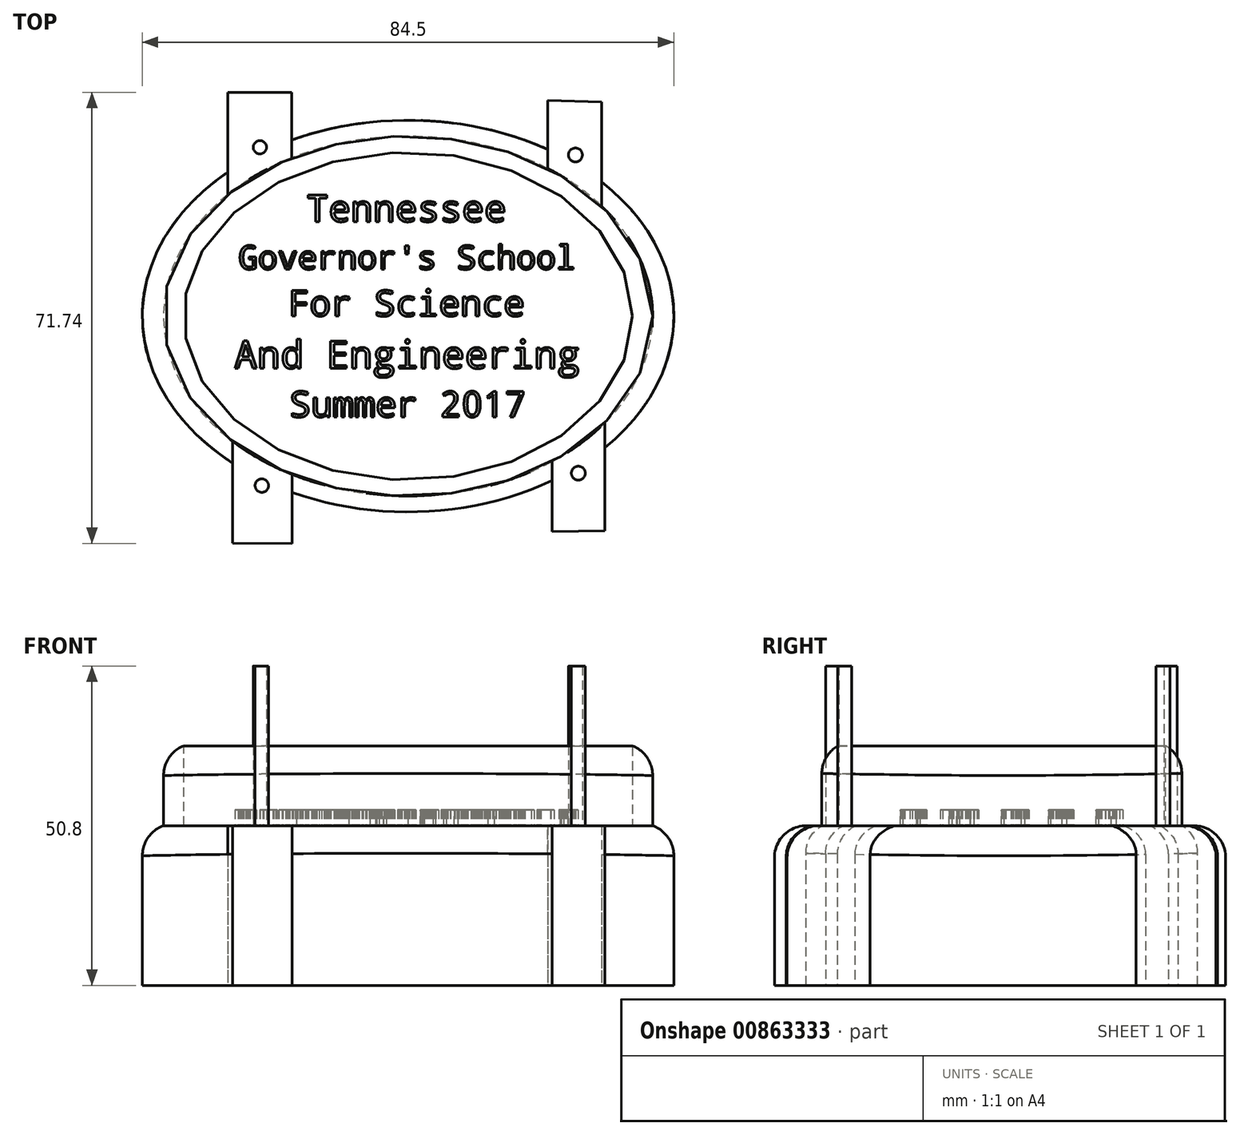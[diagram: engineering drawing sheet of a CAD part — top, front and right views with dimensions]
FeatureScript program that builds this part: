
annotation { "Feature Type Name" : "Feature", "Feature Type Description" : "" }
export const myFeature = defineFeature(function(context is Context, id is Id, definition is map)
    precondition{}
    {
        {
            var Q0;
            Q0=qCreatedBy(makeId("Top.planeOp"),FACE);
            var sketch = newSketch(context, id + "F0", { "sketchPlane" : qUnion([Q0])});
            skEllipse(sketch, "E0", {"center": v(0, 0) * mm, "majorRadius": 42.25 * mm, "minorRadius": 31.15 * mm, "majorAxis": v(1, 0)});
            skLineSegment(sketch, "E1", {"start": v(-28.66, 22.89) * mm, "end": v(-28.66, 35.59) * mm});
            skLineSegment(sketch, "E2", {"start": v(-18.5, 28) * mm, "end": v(-18.5, 35.59) * mm});
            skLineSegment(sketch, "E3", {"start": v(22.23, 26.49) * mm, "end": v(22.23, 34.32) * mm});
            skLineSegment(sketch, "E4", {"start": v(30.75, 21.36) * mm, "end": v(30.75, 34.06) * mm});
            skLineSegment(sketch, "E5", {"start": v(-27.9, -23.39) * mm, "end": v(-27.9, -36.09) * mm});
            skLineSegment(sketch, "E6", {"start": v(-18.43, -28.03) * mm, "end": v(-18.43, -36.15) * mm});
            skLineSegment(sketch, "E7", {"start": v(22.9, -26.17) * mm, "end": v(22.9, -34.3) * mm});
            skLineSegment(sketch, "E8", {"start": v(31.3, -20.93) * mm, "end": v(31.3, -34.14) * mm});
            skLineSegment(sketch, "E9", {"start": v(-28.66, 35.59) * mm, "end": v(-18.5, 35.59) * mm});
            skLineSegment(sketch, "E10", {"start": v(22.23, 34.32) * mm, "end": v(30.75, 34.06) * mm});
            skLineSegment(sketch, "E11", {"start": v(-27.9, -36.09) * mm, "end": v(-18.43, -36.15) * mm});
            skLineSegment(sketch, "E12", {"start": v(22.9, -34.3) * mm, "end": v(31.3, -34.14) * mm});
            skSolve(sketch);
        }
        {
            var Q0;
            {var subQ0=sQuery(id+"F0.wireOp",EDGE,"E0");var subQ4=makeQuery(id+"F0.imprint","INTERSECT",VERTEX,{"derivedFrom":[subQ0,sQuery(id+"F0.wireOp",EDGE,"E3")]});Q0=makeQuery(id+"F0.imprint","IMPRINT",FACE,{"disambiguationData":[TD([[makeQuery(id+"F0.imprint","IMPRINT",EDGE,{"disambiguationData":[TD([[subQ4,1.0]])],"derivedFrom":subQ0}),1.0]])]});}
            var Q1;
            {var subQ0=sQuery(id+"F0.wireOp",EDGE,"E1");Q1=makeQuery(id+"F0.imprint","IMPRINT",FACE,{"disambiguationData":[TD([[makeQuery(id+"F0.imprint","IMPRINT",EDGE,{"derivedFrom":subQ0}),-1.0]])]});}
            var Q2;
            {var subQ0=sQuery(id+"F0.wireOp",EDGE,"E3");Q2=makeQuery(id+"F0.imprint","IMPRINT",FACE,{"disambiguationData":[TD([[makeQuery(id+"F0.imprint","IMPRINT",EDGE,{"derivedFrom":subQ0}),-1.0]])]});}
            var Q3;
            {var subQ0=sQuery(id+"F0.wireOp",EDGE,"E5");Q3=makeQuery(id+"F0.imprint","IMPRINT",FACE,{"disambiguationData":[TD([[makeQuery(id+"F0.imprint","IMPRINT",EDGE,{"derivedFrom":subQ0}),1.0]])]});}
            var Q4;
            {var subQ0=sQuery(id+"F0.wireOp",EDGE,"E7");Q4=makeQuery(id+"F0.imprint","IMPRINT",FACE,{"disambiguationData":[TD([[makeQuery(id+"F0.imprint","IMPRINT",EDGE,{"derivedFrom":subQ0}),1.0]])]});}
            extrude(context, id + "F1", {"entities" : qUnion([Q0, Q1, Q2, Q3, Q4]), "depth" : 25.4 * mm, "offsetDistance" : 25.4 * mm});
        }
        {
            var Q0;
            Q0=makeQuery(id+"F1.opExtrude","CAP_FACE",FACE,{"disambiguationData":[OSD([sQuery(id+"F0.wireOp",EDGE,"E0"),sQuery(id+"F0.wireOp",EDGE,"E1"),sQuery(id+"F0.wireOp",EDGE,"E2"),sQuery(id+"F0.wireOp",EDGE,"E3"),sQuery(id+"F0.wireOp",EDGE,"E4"),sQuery(id+"F0.wireOp",EDGE,"E5"),sQuery(id+"F0.wireOp",EDGE,"E6"),sQuery(id+"F0.wireOp",EDGE,"E7"),sQuery(id+"F0.wireOp",EDGE,"E8"),sQuery(id+"F0.wireOp",EDGE,"E9"),sQuery(id+"F0.wireOp",EDGE,"E10"),sQuery(id+"F0.wireOp",EDGE,"E11"),sQuery(id+"F0.wireOp",EDGE,"E12")])],"isStart":false});
            var sketch = newSketch(context, id + "F2", { "sketchPlane" : qUnion([Q0])});
            skEllipse(sketch, "E13", {"center": v(0, 0) * mm, "majorRadius": 38.88 * mm, "minorRadius": 28.62 * mm, "majorAxis": v(1, 0)});
            skEllipse(sketch, "E14", {"center": v(0, 0) * mm, "majorRadius": 35.68 * mm, "minorRadius": 26.06 * mm, "majorAxis": v(1, 0)});
            skSolve(sketch);
        }
        {
            var Q0;
            Q0=makeQuery(id+"F2.imprint","IMPRINT",FACE,{"disambiguationData":[TD([[makeQuery(id+"F2.imprint","IMPRINT",EDGE,{"derivedFrom":sQuery(id+"F2.wireOp",EDGE,"E13")}),1.0]])]});
            extrude(context, id + "F3", {"entities" : qUnion([Q0]), "operationType" : NewBodyOperationType.ADD, "depth" : 25.4 * mm, "offsetDistance" : 25.4 * mm, "symmetric" : true});
        }
        {
            var Q0;
            Q0=makeQuery(id+"F3.opExtrude","CAP_EDGE",EDGE,{"disambiguationData":[OSD([sQuery(id+"F2.wireOp",EDGE,"E13")])],"isStart":false});
            var Q1;
            {var subQ0=sQuery(id+"F0.wireOp",EDGE,"E0");Q1=makeQuery(id+"F1.opExtrude","CAP_EDGE",EDGE,{"disambiguationData":[OSD([subQ0]),TDD([makeQuery(id+"F0.imprint","IMPRINT",EDGE,{"disambiguationData":[TD([[makeQuery(id+"F0.imprint","INTERSECT",VERTEX,{"derivedFrom":[subQ0,sQuery(id+"F0.wireOp",EDGE,"E1")]}),-1.0]])],"derivedFrom":subQ0})])],"isStart":false});}
            fillet(context, id + "F4", {"entities" : qUnion([Q0, Q1]), "radius" : 5.08 * mm, "tangentPropagation" : true, "allowEdgeOverflow" : false});
        }
        {
            var Q0;
            Q0=makeQuery(id+"F1.opExtrude","CAP_EDGE",EDGE,{"disambiguationData":[OSD([sQuery(id+"F0.wireOp",EDGE,"E11")])],"isStart":false});
            fillet(context, id + "F5", {"entities" : qUnion([Q0]), "radius" : 5.08 * mm, "tangentPropagation" : true, "allowEdgeOverflow" : false});
        }
        {
            var Q0;
            Q0=makeQuery(id+"F1.opExtrude","CAP_EDGE",EDGE,{"disambiguationData":[OSD([sQuery(id+"F0.wireOp",EDGE,"E12")])],"isStart":false});
            fillet(context, id + "F6", {"entities" : qUnion([Q0]), "radius" : 5.08 * mm, "tangentPropagation" : true, "allowEdgeOverflow" : false});
        }
        {
            var Q0;
            Q0=makeQuery(id+"F1.opExtrude","CAP_EDGE",EDGE,{"disambiguationData":[OSD([sQuery(id+"F0.wireOp",EDGE,"E10")])],"isStart":false});
            fillet(context, id + "F7", {"entities" : qUnion([Q0]), "radius" : 5.08 * mm, "tangentPropagation" : true, "allowEdgeOverflow" : false});
        }
        {
            var Q0;
            Q0=makeQuery(id+"F1.opExtrude","CAP_EDGE",EDGE,{"disambiguationData":[OSD([sQuery(id+"F0.wireOp",EDGE,"E9")])],"isStart":false});
            fillet(context, id + "F8", {"entities" : qUnion([Q0]), "radius" : 5.08 * mm, "tangentPropagation" : true, "allowEdgeOverflow" : false});
        }
        {
            var Q0;
            {var subQ0=sQuery(id+"F0.wireOp",EDGE,"E0");Q0=makeQuery(id+"F1.opExtrude","CAP_EDGE",EDGE,{"disambiguationData":[OSD([subQ0]),TDD([makeQuery(id+"F0.imprint","IMPRINT",EDGE,{"disambiguationData":[TD([[makeQuery(id+"F0.imprint","INTERSECT",VERTEX,{"derivedFrom":[subQ0,sQuery(id+"F0.wireOp",EDGE,"E6")]}),-1.0]])],"derivedFrom":subQ0})])],"isStart":false});}
            fillet(context, id + "F9", {"entities" : qUnion([Q0]), "radius" : 5.08 * mm, "tangentPropagation" : true, "allowEdgeOverflow" : false});
        }
        {
            var Q0;
            {var subQ0=sQuery(id+"F0.wireOp",EDGE,"E0");Q0=makeQuery(id+"F1.opExtrude","CAP_EDGE",EDGE,{"disambiguationData":[OSD([subQ0]),TDD([makeQuery(id+"F0.imprint","IMPRINT",EDGE,{"disambiguationData":[TD([[makeQuery(id+"F0.imprint","INTERSECT",VERTEX,{"derivedFrom":[subQ0,sQuery(id+"F0.wireOp",EDGE,"E4")]}),1.0]])],"derivedFrom":subQ0})])],"isStart":false});}
            fillet(context, id + "F10", {"entities" : qUnion([Q0]), "radius" : 5.08 * mm, "tangentPropagation" : true, "allowEdgeOverflow" : false});
        }
        {
            var Q0;
            {var subQ0=sQuery(id+"F0.wireOp",EDGE,"E0");Q0=makeQuery(id+"F1.opExtrude","CAP_EDGE",EDGE,{"disambiguationData":[OSD([subQ0]),TDD([makeQuery(id+"F0.imprint","IMPRINT",EDGE,{"disambiguationData":[TD([[makeQuery(id+"F0.imprint","INTERSECT",VERTEX,{"derivedFrom":[subQ0,sQuery(id+"F0.wireOp",EDGE,"E2")]}),1.0]])],"derivedFrom":subQ0})])],"isStart":false});}
            fillet(context, id + "F11", {"entities" : qUnion([Q0]), "radius" : 5.08 * mm, "tangentPropagation" : true, "allowEdgeOverflow" : false});
        }
        {
            var Q0;
            {var subQ0=sQuery(id+"F0.wireOp",EDGE,"E5");var subQ1=sQuery(id+"F0.wireOp",EDGE,"E4");var subQ2=sQuery(id+"F0.wireOp",EDGE,"E3");var subQ3=sQuery(id+"F0.wireOp",EDGE,"E2");var subQ4=sQuery(id+"F0.wireOp",EDGE,"E1");var subQ5=sQuery(id+"F0.wireOp",EDGE,"E6");var subQ6=sQuery(id+"F0.wireOp",EDGE,"E0");var subQ7=sQuery(id+"F0.wireOp",EDGE,"E8");var subQ8=sQuery(id+"F0.wireOp",EDGE,"E7");var subQ9=sQuery(id+"F0.wireOp",EDGE,"E9");var subQ10=sQuery(id+"F0.wireOp",EDGE,"E10");var subQ11=sQuery(id+"F0.wireOp",EDGE,"E11");var subQ12=sQuery(id+"F0.wireOp",EDGE,"E12");Q0=makeQuery(id+"F9.opFillet","SPLIT",FACE,{"disambiguationData":[OD(1.0)],"derivedFrom":makeQuery(id+"F3.boolean.opBoolean","SPLIT",FACE,{"disambiguationData":[TD([makeQuery(id+"F1.opExtrude","SWEPT_FACE",FACE,{"disambiguationData":[OSD([subQ4])]})])],"derivedFrom":makeQuery(id+"F1.opExtrude","CAP_FACE",FACE,{"disambiguationData":[OSD([subQ6,subQ4,subQ3,subQ2,subQ1,subQ0,subQ5,subQ8,subQ7,subQ9,subQ10,subQ11,subQ12])],"isStart":false})})});}
            var sketch = newSketch(context, id + "F12", { "sketchPlane" : qUnion([Q0])});
            skCircle(sketch, "E15", {"center": v(-23.25, -26.96) * mm, "radius": 1.07 * mm});
            skSolve(sketch);
        }
        {
            var Q0;
            Q0=makeQuery(id+"F12.imprint","IMPRINT",FACE,{"disambiguationData":[TD([[makeQuery(id+"F12.imprint","IMPRINT",EDGE,{"derivedFrom":sQuery(id+"F12.wireOp",EDGE,"E15")}),1.0]])]});
            extrude(context, id + "F13", {"entities" : qUnion([Q0]), "operationType" : NewBodyOperationType.ADD, "depth" : 25.4 * mm, "offsetDistance" : 25.4 * mm});
        }
        {
            var Q0;
            {var subQ0=sQuery(id+"F0.wireOp",EDGE,"E5");var subQ1=sQuery(id+"F0.wireOp",EDGE,"E4");var subQ2=sQuery(id+"F0.wireOp",EDGE,"E3");var subQ3=sQuery(id+"F0.wireOp",EDGE,"E2");var subQ4=sQuery(id+"F0.wireOp",EDGE,"E1");var subQ5=sQuery(id+"F0.wireOp",EDGE,"E6");var subQ6=sQuery(id+"F0.wireOp",EDGE,"E0");var subQ7=sQuery(id+"F0.wireOp",EDGE,"E8");var subQ8=sQuery(id+"F0.wireOp",EDGE,"E7");var subQ9=sQuery(id+"F0.wireOp",EDGE,"E9");var subQ10=sQuery(id+"F0.wireOp",EDGE,"E10");var subQ11=sQuery(id+"F0.wireOp",EDGE,"E11");var subQ12=sQuery(id+"F0.wireOp",EDGE,"E12");Q0=makeQuery(id+"F11.opFillet","SPLIT",FACE,{"disambiguationData":[OD(1.0)],"derivedFrom":makeQuery(id+"F10.opFillet","SPLIT",FACE,{"disambiguationData":[OD(0.0)],"derivedFrom":makeQuery(id+"F9.opFillet","SPLIT",FACE,{"disambiguationData":[OD(0.0)],"derivedFrom":makeQuery(id+"F3.boolean.opBoolean","SPLIT",FACE,{"disambiguationData":[TD([makeQuery(id+"F1.opExtrude","SWEPT_FACE",FACE,{"disambiguationData":[OSD([subQ4])]})])],"derivedFrom":makeQuery(id+"F1.opExtrude","CAP_FACE",FACE,{"disambiguationData":[OSD([subQ6,subQ4,subQ3,subQ2,subQ1,subQ0,subQ5,subQ8,subQ7,subQ9,subQ10,subQ11,subQ12])],"isStart":false})})})})});}
            var sketch = newSketch(context, id + "F14", { "sketchPlane" : qUnion([Q0])});
            skCircle(sketch, "E16", {"center": v(-23.56, 26.85) * mm, "radius": 1.06 * mm});
            skSolve(sketch);
        }
        {
            var Q0;
            Q0=makeQuery(id+"F14.imprint","IMPRINT",FACE,{"disambiguationData":[TD([[makeQuery(id+"F14.imprint","IMPRINT",EDGE,{"derivedFrom":sQuery(id+"F14.wireOp",EDGE,"E16")}),1.0]])]});
            extrude(context, id + "F15", {"entities" : qUnion([Q0]), "operationType" : NewBodyOperationType.ADD, "depth" : 25.4 * mm, "offsetDistance" : 25.4 * mm});
        }
        {
            var Q0;
            {var subQ0=sQuery(id+"F0.wireOp",EDGE,"E5");var subQ1=sQuery(id+"F0.wireOp",EDGE,"E4");var subQ2=sQuery(id+"F0.wireOp",EDGE,"E3");var subQ3=sQuery(id+"F0.wireOp",EDGE,"E2");var subQ4=sQuery(id+"F0.wireOp",EDGE,"E1");var subQ5=sQuery(id+"F0.wireOp",EDGE,"E6");var subQ6=sQuery(id+"F0.wireOp",EDGE,"E0");var subQ7=sQuery(id+"F0.wireOp",EDGE,"E8");var subQ8=sQuery(id+"F0.wireOp",EDGE,"E7");var subQ9=sQuery(id+"F0.wireOp",EDGE,"E9");var subQ10=sQuery(id+"F0.wireOp",EDGE,"E10");var subQ11=sQuery(id+"F0.wireOp",EDGE,"E11");var subQ12=sQuery(id+"F0.wireOp",EDGE,"E12");Q0=makeQuery(id+"F11.opFillet","SPLIT",FACE,{"disambiguationData":[OD(0.0)],"derivedFrom":makeQuery(id+"F10.opFillet","SPLIT",FACE,{"disambiguationData":[OD(0.0)],"derivedFrom":makeQuery(id+"F9.opFillet","SPLIT",FACE,{"disambiguationData":[OD(0.0)],"derivedFrom":makeQuery(id+"F3.boolean.opBoolean","SPLIT",FACE,{"disambiguationData":[TD([makeQuery(id+"F1.opExtrude","SWEPT_FACE",FACE,{"disambiguationData":[OSD([subQ4])]})])],"derivedFrom":makeQuery(id+"F1.opExtrude","CAP_FACE",FACE,{"disambiguationData":[OSD([subQ6,subQ4,subQ3,subQ2,subQ1,subQ0,subQ5,subQ8,subQ7,subQ9,subQ10,subQ11,subQ12])],"isStart":false})})})})});}
            var sketch = newSketch(context, id + "F16", { "sketchPlane" : qUnion([Q0])});
            skCircle(sketch, "E17", {"center": v(26.61, 25.63) * mm, "radius": 1.1 * mm});
            skSolve(sketch);
        }
        {
            var Q0;
            Q0=makeQuery(id+"F16.imprint","IMPRINT",FACE,{"disambiguationData":[TD([[makeQuery(id+"F16.imprint","IMPRINT",EDGE,{"derivedFrom":sQuery(id+"F16.wireOp",EDGE,"E17")}),1.0]])]});
            extrude(context, id + "F17", {"entities" : qUnion([Q0]), "operationType" : NewBodyOperationType.ADD, "depth" : 25.4 * mm, "offsetDistance" : 25.4 * mm});
        }
        {
            var Q0;
            {var subQ0=sQuery(id+"F0.wireOp",EDGE,"E5");var subQ1=sQuery(id+"F0.wireOp",EDGE,"E4");var subQ2=sQuery(id+"F0.wireOp",EDGE,"E3");var subQ3=sQuery(id+"F0.wireOp",EDGE,"E2");var subQ4=sQuery(id+"F0.wireOp",EDGE,"E1");var subQ5=sQuery(id+"F0.wireOp",EDGE,"E6");var subQ6=sQuery(id+"F0.wireOp",EDGE,"E0");var subQ7=sQuery(id+"F0.wireOp",EDGE,"E8");var subQ8=sQuery(id+"F0.wireOp",EDGE,"E7");var subQ9=sQuery(id+"F0.wireOp",EDGE,"E9");var subQ10=sQuery(id+"F0.wireOp",EDGE,"E10");var subQ11=sQuery(id+"F0.wireOp",EDGE,"E11");var subQ12=sQuery(id+"F0.wireOp",EDGE,"E12");Q0=makeQuery(id+"F10.opFillet","SPLIT",FACE,{"disambiguationData":[OD(1.0)],"derivedFrom":makeQuery(id+"F9.opFillet","SPLIT",FACE,{"disambiguationData":[OD(0.0)],"derivedFrom":makeQuery(id+"F3.boolean.opBoolean","SPLIT",FACE,{"disambiguationData":[TD([makeQuery(id+"F1.opExtrude","SWEPT_FACE",FACE,{"disambiguationData":[OSD([subQ4])]})])],"derivedFrom":makeQuery(id+"F1.opExtrude","CAP_FACE",FACE,{"disambiguationData":[OSD([subQ6,subQ4,subQ3,subQ2,subQ1,subQ0,subQ5,subQ8,subQ7,subQ9,subQ10,subQ11,subQ12])],"isStart":false})})})});}
            var sketch = newSketch(context, id + "F18", { "sketchPlane" : qUnion([Q0])});
            skCircle(sketch, "E18", {"center": v(27.07, -24.99) * mm, "radius": 1.1 * mm});
            skSolve(sketch);
        }
        {
            var Q0;
            Q0=makeQuery(id+"F18.imprint","IMPRINT",FACE,{"disambiguationData":[TD([[makeQuery(id+"F18.imprint","IMPRINT",EDGE,{"derivedFrom":sQuery(id+"F18.wireOp",EDGE,"E18")}),1.0]])]});
            extrude(context, id + "F19", {"entities" : qUnion([Q0]), "operationType" : NewBodyOperationType.ADD, "depth" : 25.4 * mm, "offsetDistance" : 25.4 * mm});
        }
        {
            var Q0;
            Q0=makeQuery(id+"F3.boolean.opBoolean","SPLIT",FACE,{"disambiguationData":[TD([makeQuery(id+"F3.opExtrude","SWEPT_FACE",FACE,{"disambiguationData":[OSD([sQuery(id+"F2.wireOp",EDGE,"E14")])]})])],"derivedFrom":makeQuery(id+"F1.opExtrude","CAP_FACE",FACE,{"disambiguationData":[OSD([sQuery(id+"F0.wireOp",EDGE,"E0"),sQuery(id+"F0.wireOp",EDGE,"E1"),sQuery(id+"F0.wireOp",EDGE,"E2"),sQuery(id+"F0.wireOp",EDGE,"E3"),sQuery(id+"F0.wireOp",EDGE,"E4"),sQuery(id+"F0.wireOp",EDGE,"E5"),sQuery(id+"F0.wireOp",EDGE,"E6"),sQuery(id+"F0.wireOp",EDGE,"E7"),sQuery(id+"F0.wireOp",EDGE,"E8"),sQuery(id+"F0.wireOp",EDGE,"E9"),sQuery(id+"F0.wireOp",EDGE,"E10"),sQuery(id+"F0.wireOp",EDGE,"E11"),sQuery(id+"F0.wireOp",EDGE,"E12")])],"isStart":false})});
            var sketch = newSketch(context, id + "F20", { "sketchPlane" : qUnion([Q0])});
            skText(sketch, "E19", { "text": "Tennessee", "fontName": "DroidSansMono.ttf"});
            skText(sketch, "E20", { "text": "Governor\'s School", "fontName": "DroidSansMono.ttf"});
            skText(sketch, "E21", { "text": "For Science", "fontName": "DroidSansMono.ttf"});
            skText(sketch, "E22", { "text": "And Engineering", "fontName": "DroidSansMono.ttf"});
            skText(sketch, "E23", { "text": "Summer 2017", "fontName": "DroidSansMono.ttf"});
            const initialGuessF20  = {"E19": [-0.01617, 0.01502, 1, 0, 0.00424], "E20": [-0.02703, 0.00745, 1, 0, 0.00379], "E21": [-0.0191, 0, 1, 0, 0.00411], "E22": [-0.02765, -0.00832, 1, 0, 0.0044], "E23": [-0.01886, -0.01605, 1, 0, 0.0041]};
            skSetInitialGuess(sketch, initialGuessF20);
            skSolve(sketch);
        }
        {
            var Q0;
            Q0 = qSketchRegion(id + "F20", true);
            extrude(context, id + "F21", {"entities" : qUnion([Q0]), "operationType" : NewBodyOperationType.ADD, "depth" : 2.54 * mm, "offsetDistance" : 25.4 * mm});
        }
    });
